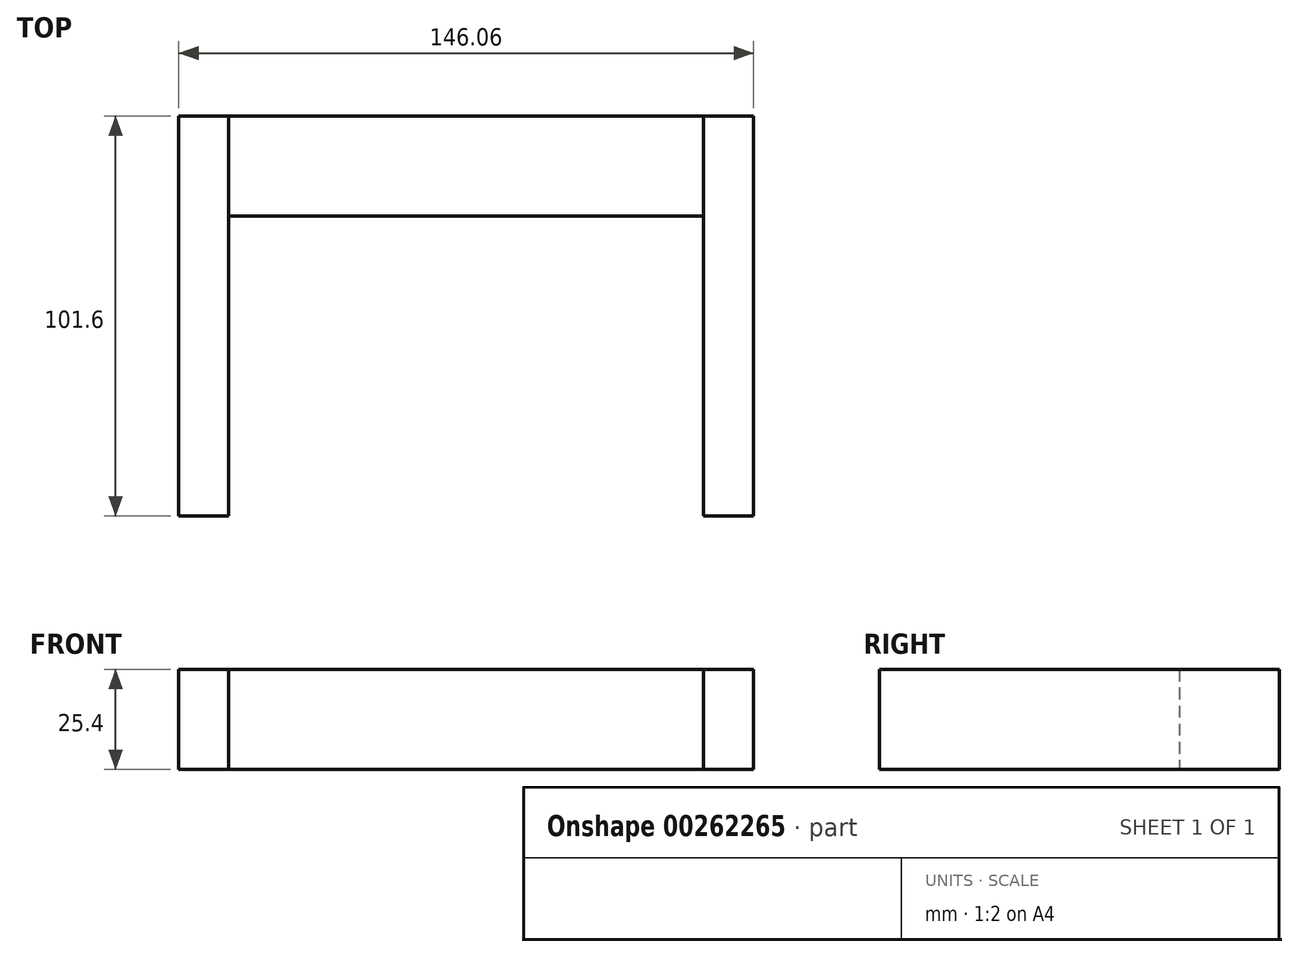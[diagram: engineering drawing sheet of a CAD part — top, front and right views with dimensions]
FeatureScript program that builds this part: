
annotation { "Feature Type Name" : "Feature", "Feature Type Description" : "" }
export const myFeature = defineFeature(function(context is Context, id is Id, definition is map)
    precondition{}
    {
        {
            var Q0;
            Q0=qCreatedBy(makeId("Front.planeOp"),FACE);
            var sketch = newSketch(context, id + "F0", { "sketchPlane" : qUnion([Q0])});
            skLineSegment(sketch, "E0.bottom", {"start": v(60.33, 12.7) * mm, "end": v(-60.33, 12.7) * mm});
            skLineSegment(sketch, "E0.top", {"start": v(60.33, -12.7) * mm, "end": v(-60.33, -12.7) * mm});
            skLineSegment(sketch, "E0.left", {"start": v(60.33, 12.7) * mm, "end": v(60.33, -12.7) * mm});
            skLineSegment(sketch, "E0.right", {"start": v(-60.33, 12.7) * mm, "end": v(-60.33, -12.7) * mm});
            skPoint(sketch, "E0.middle", {"position": v(0, 0) * mm});
            skLineSegment(sketch, "E1.bottom", {"start": v(-60.33, 12.7) * mm, "end": v(-73.03, 12.7) * mm});
            skLineSegment(sketch, "E1.top", {"start": v(-60.32, -12.7) * mm, "end": v(-73.03, -12.7) * mm});
            skLineSegment(sketch, "E1.right", {"start": v(-73.03, 12.7) * mm, "end": v(-73.03, -12.7) * mm});
            skLineSegment(sketch, "E2.bottom", {"start": v(60.33, -12.7) * mm, "end": v(73.03, -12.7) * mm});
            skLineSegment(sketch, "E2.top", {"start": v(60.33, 12.7) * mm, "end": v(73.03, 12.7) * mm});
            skLineSegment(sketch, "E2.left", {"start": v(60.33, -12.7) * mm, "end": v(60.33, 12.7) * mm});
            skLineSegment(sketch, "E2.right", {"start": v(73.03, -12.7) * mm, "end": v(73.03, 12.7) * mm});
            skSolve(sketch);
        }
        {
            var Q0;
            Q0=makeQuery(id+"F0.imprint","IMPRINT",FACE,{"disambiguationData":[TD([[makeQuery(id+"F0.imprint","IMPRINT",EDGE,{"derivedFrom":sQuery(id+"F0.wireOp",EDGE,"E0.bottom")}),1.0]])]});
            extrude(context, id + "F1", {"entities" : qUnion([Q0]), "depth" : 25.4 * mm});
        }
        {
            var Q0;
            Q0=makeQuery(id+"F0.imprint","IMPRINT",FACE,{"disambiguationData":[TD([[makeQuery(id+"F0.imprint","IMPRINT",EDGE,{"derivedFrom":sQuery(id+"F0.wireOp",EDGE,"E1.bottom")}),1.0]])]});
            var Q1;
            Q1=makeQuery(id+"F0.imprint","IMPRINT",FACE,{"disambiguationData":[TD([[makeQuery(id+"F0.imprint","IMPRINT",EDGE,{"derivedFrom":sQuery(id+"F0.wireOp",EDGE,"E2.bottom")}),1.0]])]});
            extrude(context, id + "F2", {"entities" : qUnion([Q0, Q1]), "depth" : 101.6 * mm});
        }
    });
